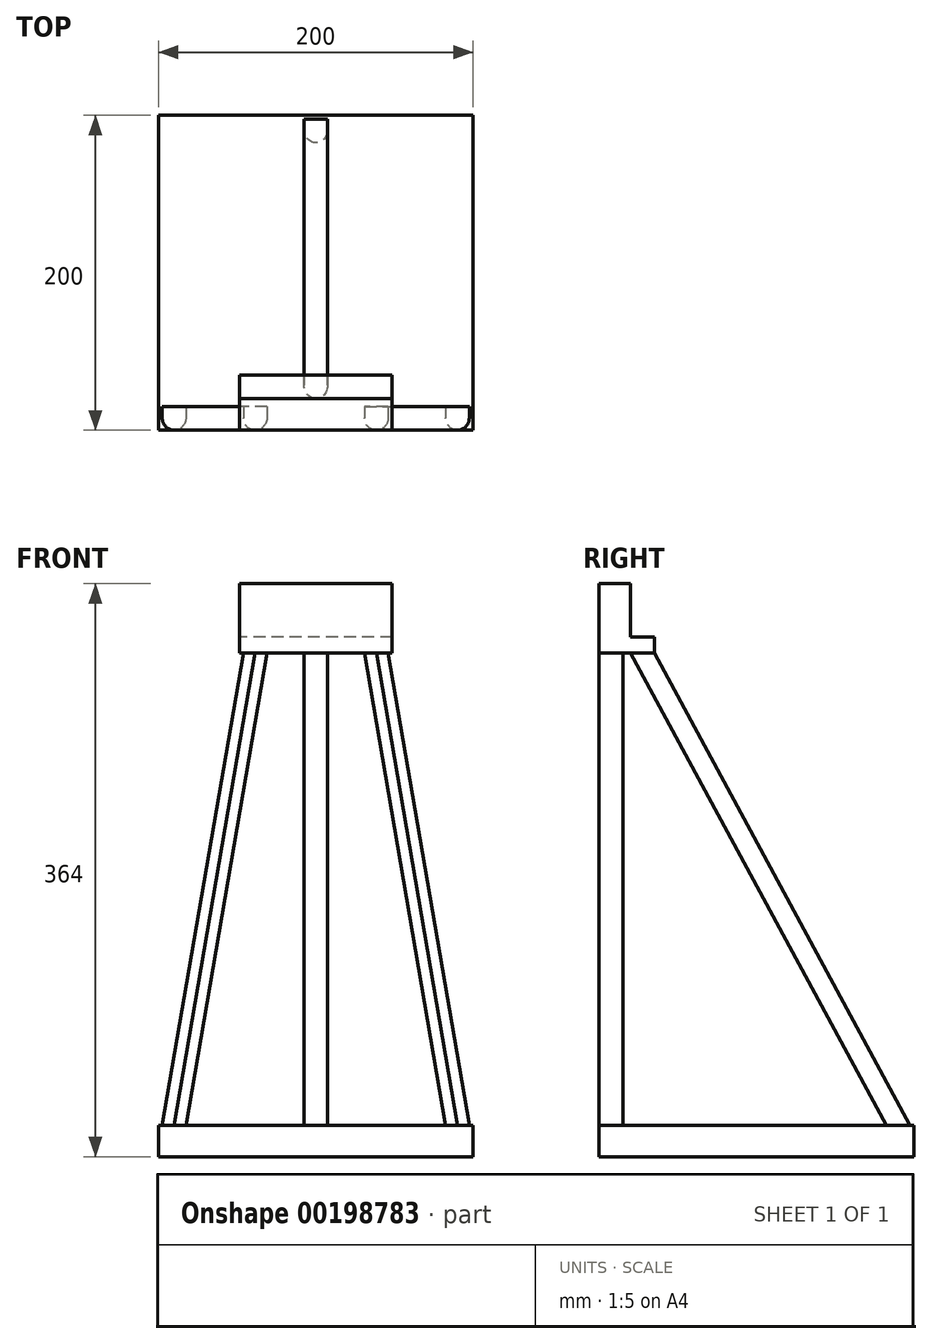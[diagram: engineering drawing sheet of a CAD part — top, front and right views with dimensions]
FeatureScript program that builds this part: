
annotation { "Feature Type Name" : "Feature", "Feature Type Description" : "" }
export const myFeature = defineFeature(function(context is Context, id is Id, definition is map)
    precondition{}
    {
        {
            var Q0;
            Q0=qCreatedBy(makeId("Top.planeOp"),FACE);
            var sketch = newSketch(context, id + "F0", { "sketchPlane" : qUnion([Q0])});
            skLineSegment(sketch, "E0.bottom", {"start": v(100, 100) * mm, "end": v(-100, 100) * mm});
            skLineSegment(sketch, "E0.top", {"start": v(100, -100) * mm, "end": v(-100, -100) * mm});
            skLineSegment(sketch, "E0.left", {"start": v(100, 100) * mm, "end": v(100, -100) * mm});
            skLineSegment(sketch, "E0.right", {"start": v(-100, 100) * mm, "end": v(-100, -100) * mm});
            skPoint(sketch, "E0.middle", {"position": v(0, 0) * mm});
            skSolve(sketch);
        }
        {
            var Q0;
            Q0=makeQuery(id+"F0.imprint","IMPRINT",FACE,{"disambiguationData":[TD([[makeQuery(id+"F0.imprint","IMPRINT",EDGE,{"derivedFrom":sQuery(id+"F0.wireOp",EDGE,"E0.bottom")}),1.0]])]});
            extrude(context, id + "F1", {"entities" : qUnion([Q0]), "endBound" : BoundingType.SYMMETRIC, "depth" : 20 * mm});
        }
        {
            var Q0;
            Q0=qCreatedBy(makeId("Right.planeOp"),FACE);
            var sketch = newSketch(context, id + "F2", { "sketchPlane" : qUnion([Q0])});
            skLineSegment(sketch, "E1.bottom", {"start": v(0, 0) * mm, "end": v(-20, 0) * mm});
            skLineSegment(sketch, "E1.top", {"start": v(0, 34) * mm, "end": v(-20, 34) * mm});
            skLineSegment(sketch, "E1.left", {"start": v(0, 0) * mm, "end": v(0, 34) * mm});
            skLineSegment(sketch, "E1.right", {"start": v(-20, 0) * mm, "end": v(-20, 34) * mm});
            skLineSegment(sketch, "E2.bottom", {"start": v(-20, 0) * mm, "end": v(15, 0) * mm});
            skLineSegment(sketch, "E2.top", {"start": v(-20, -10) * mm, "end": v(15, -10) * mm});
            skLineSegment(sketch, "E2.left", {"start": v(-20, 0) * mm, "end": v(-20, -10) * mm});
            skLineSegment(sketch, "E2.right", {"start": v(15, 0) * mm, "end": v(15, -10) * mm});
            skSolve(sketch);
        }
        {
            var Q0;
            Q0 = qSketchRegion(id + "F2", true);
            extrude(context, id + "F3", {"entities" : qUnion([Q0]), "endBound" : BoundingType.SYMMETRIC, "depth" : 97 * mm});
        }
        {
            var Q0;
            Q0=makeQuery(id+"F3.opExtrude","SWEPT_BODY",BODY,{"disambiguationData":[OSD([sQuery(id+"F2.wireOp",EDGE,"E1.top"),sQuery(id+"F2.wireOp",EDGE,"E1.left"),sQuery(id+"F2.wireOp",EDGE,"E1.right"),sQuery(id+"F2.wireOp",EDGE,"E2.bottom"),sQuery(id+"F2.wireOp",EDGE,"E2.top"),sQuery(id+"F2.wireOp",EDGE,"E2.left"),sQuery(id+"F2.wireOp",EDGE,"E2.right")])]});
            transform(context, id + "F4", {"entities" : qUnion([Q0]), "transformType" : TransformType.TRANSLATION_3D, "dx" : 0 * mm, "dy" : -80 * mm, "dz" : 320 * mm, "makeCopy" : false});
        }
        {
            var Q0;
            Q0=makeQuery(id+"F3.opExtrude","SWEPT_FACE",FACE,{"disambiguationData":[OSD([sQuery(id+"F2.wireOp",EDGE,"E2.top")])]});
            var sketch = newSketch(context, id + "F5", { "sketchPlane" : qUnion([Q0])});
            skLineSegment(sketch, "E3.bottom", {"start": v(-31, 85) * mm, "end": v(-46, 85) * mm});
            skLineSegment(sketch, "E3.top", {"start": v(-31, 100) * mm, "end": v(-46, 100) * mm});
            skLineSegment(sketch, "E3.left", {"start": v(-31, 85) * mm, "end": v(-31, 100) * mm});
            skLineSegment(sketch, "E3.right", {"start": v(-46, 85) * mm, "end": v(-46, 100) * mm});
            skPoint(sketch, "E3.middle", {"position": v(-38.5, 92.5) * mm});
            skLineSegment(sketch, "E4.bottom", {"start": v(46, 85) * mm, "end": v(31, 85) * mm});
            skLineSegment(sketch, "E4.top", {"start": v(46, 100) * mm, "end": v(31, 100) * mm});
            skLineSegment(sketch, "E4.left", {"start": v(46, 85) * mm, "end": v(46, 100) * mm});
            skLineSegment(sketch, "E4.right", {"start": v(31, 85) * mm, "end": v(31, 100) * mm});
            skPoint(sketch, "E4.middle", {"position": v(38.5, 92.5) * mm});
            skLineSegment(sketch, "E5.bottom", {"start": v(7.5, 65) * mm, "end": v(-7.5, 65) * mm});
            skLineSegment(sketch, "E5.top", {"start": v(7.5, 80) * mm, "end": v(-7.5, 80) * mm});
            skLineSegment(sketch, "E5.left", {"start": v(7.5, 65) * mm, "end": v(7.5, 80) * mm});
            skLineSegment(sketch, "E5.right", {"start": v(-7.5, 65) * mm, "end": v(-7.5, 80) * mm});
            skPoint(sketch, "E5.middle", {"position": v(0, 72.5) * mm});
            skSolve(sketch);
        }
        {
            var Q0;
            Q0=makeQuery(id+"F3.opExtrude","SWEPT_FACE",FACE,{"disambiguationData":[OSD([sQuery(id+"F2.wireOp",EDGE,"E1.right"),sQuery(id+"F2.wireOp",EDGE,"E2.left")])]});
            var sketch = newSketch(context, id + "F6", { "sketchPlane" : qUnion([Q0])});
            skLineSegment(sketch, "E6", {"start": v(-38.5, 310) * mm, "end": v(-90, 10) * mm});
            skLineSegment(sketch, "E7", {"start": v(38.5, 310) * mm, "end": v(90, 10) * mm});
            skSolve(sketch);
        }
        {
            var Q0;
            Q0=makeQuery(id+"F5.imprint","IMPRINT",FACE,{"disambiguationData":[TD([[makeQuery(id+"F5.imprint","IMPRINT",EDGE,{"derivedFrom":sQuery(id+"F5.wireOp",EDGE,"E3.bottom")}),-1.0]])]});
            var Q1;
            Q1=sQuery(id+"F6.wireOp",EDGE,"E6");
            sweep(context, id + "F7", {"profiles" : qUnion([Q0]), "path" : qUnion([Q1])});
        }
        {
            var Q0;
            Q0=makeQuery(id+"F5.imprint","IMPRINT",FACE,{"disambiguationData":[TD([[makeQuery(id+"F5.imprint","IMPRINT",EDGE,{"derivedFrom":sQuery(id+"F5.wireOp",EDGE,"E4.bottom")}),-1.0]])]});
            var Q1;
            Q1=sQuery(id+"F6.wireOp",EDGE,"E7");
            sweep(context, id + "F8", {"profiles" : qUnion([Q0]), "path" : qUnion([Q1])});
        }
        {
            var Q0;
            Q0=qCreatedBy(makeId("Right.planeOp"),FACE);
            var sketch = newSketch(context, id + "F9", { "sketchPlane" : qUnion([Q0])});
            skLineSegment(sketch, "E8", {"start": v(-72.5, 310) * mm, "end": v(90, 10) * mm});
            skSolve(sketch);
        }
        {
            var Q0;
            Q0=makeQuery(id+"F5.imprint","IMPRINT",FACE,{"disambiguationData":[TD([[makeQuery(id+"F5.imprint","IMPRINT",EDGE,{"derivedFrom":sQuery(id+"F5.wireOp",EDGE,"E5.bottom")}),-1.0]])]});
            var Q1;
            Q1=sQuery(id+"F9.wireOp",EDGE,"E8");
            sweep(context, id + "F10", {"profiles" : qUnion([Q0]), "path" : qUnion([Q1])});
        }
        {
            var Q0;
            Q0=makeQuery(id+"F7.opSweep","SWEPT_EDGE",EDGE,{"disambiguationData":[OSD([sQuery(id+"F2.wireOp",EDGE,"E2.top"),sQuery(id+"F2.wireOp",EDGE,"E2.left"),sQuery(id+"F5.wireOp",EDGE,"E3.top"),sQuery(id+"F5.wireOp",EDGE,"E3.right"),sQuery(id+"F6.wireOp",EDGE,"E6")])]});
            var Q1;
            Q1=makeQuery(id+"F7.opSweep","SWEPT_EDGE",EDGE,{"disambiguationData":[OSD([sQuery(id+"F2.wireOp",EDGE,"E2.top"),sQuery(id+"F2.wireOp",EDGE,"E2.left"),sQuery(id+"F5.wireOp",EDGE,"E3.top"),sQuery(id+"F5.wireOp",EDGE,"E3.left"),sQuery(id+"F6.wireOp",EDGE,"E6")])]});
            var Q2;
            Q2=makeQuery(id+"F10.opSweep","SWEPT_EDGE",EDGE,{"disambiguationData":[OSD([sQuery(id+"F5.wireOp",EDGE,"E5.top"),sQuery(id+"F5.wireOp",EDGE,"E5.right"),sQuery(id+"F9.wireOp",EDGE,"E8")])]});
            var Q3;
            Q3=makeQuery(id+"F8.opSweep","SWEPT_EDGE",EDGE,{"disambiguationData":[OSD([sQuery(id+"F2.wireOp",EDGE,"E2.top"),sQuery(id+"F2.wireOp",EDGE,"E2.left"),sQuery(id+"F5.wireOp",EDGE,"E4.top"),sQuery(id+"F5.wireOp",EDGE,"E4.right"),sQuery(id+"F6.wireOp",EDGE,"E7")])]});
            var Q4;
            Q4=makeQuery(id+"F8.opSweep","SWEPT_EDGE",EDGE,{"disambiguationData":[OSD([sQuery(id+"F2.wireOp",EDGE,"E2.top"),sQuery(id+"F2.wireOp",EDGE,"E2.left"),sQuery(id+"F5.wireOp",EDGE,"E4.top"),sQuery(id+"F5.wireOp",EDGE,"E4.left"),sQuery(id+"F6.wireOp",EDGE,"E7")])]});
            var Q5;
            Q5=makeQuery(id+"F10.opSweep","SWEPT_EDGE",EDGE,{"disambiguationData":[OSD([sQuery(id+"F5.wireOp",EDGE,"E5.top"),sQuery(id+"F5.wireOp",EDGE,"E5.left"),sQuery(id+"F9.wireOp",EDGE,"E8")])]});
            fillet(context, id + "F11", {"entities" : qUnion([Q0, Q1, Q2, Q3, Q4, Q5]), "radius" : 7.5 * mm, "tangentPropagation" : true, "allowEdgeOverflow" : false});
        }
    });
